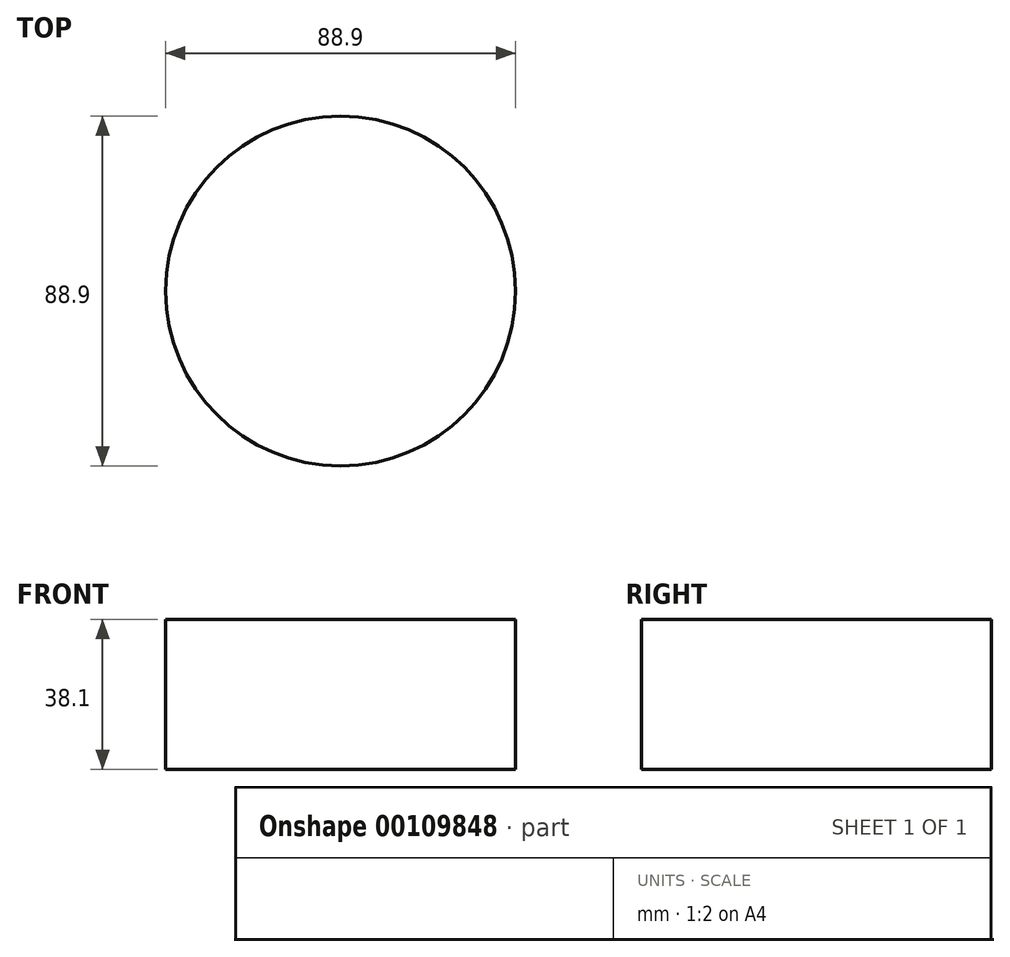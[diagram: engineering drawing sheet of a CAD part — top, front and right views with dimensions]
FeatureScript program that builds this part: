
annotation { "Feature Type Name" : "Feature", "Feature Type Description" : "" }
export const myFeature = defineFeature(function(context is Context, id is Id, definition is map)
    precondition{}
    {
        {
            var Q0;
            Q0=qCreatedBy(makeId("Top.planeOp"),FACE);
            var sketch = newSketch(context, id + "F0", { "sketchPlane" : qUnion([Q0])});
            skCircle(sketch, "E0", {"center": v(0, 0) * mm, "radius": 44.45 * mm});
            skSolve(sketch);
        }
        {
            var Q0;
            Q0 = qSketchRegion(id + "F0", true);
            extrude(context, id + "F1", {"entities" : qUnion([Q0]), "depth" : 38.1 * mm});
        }
    });
